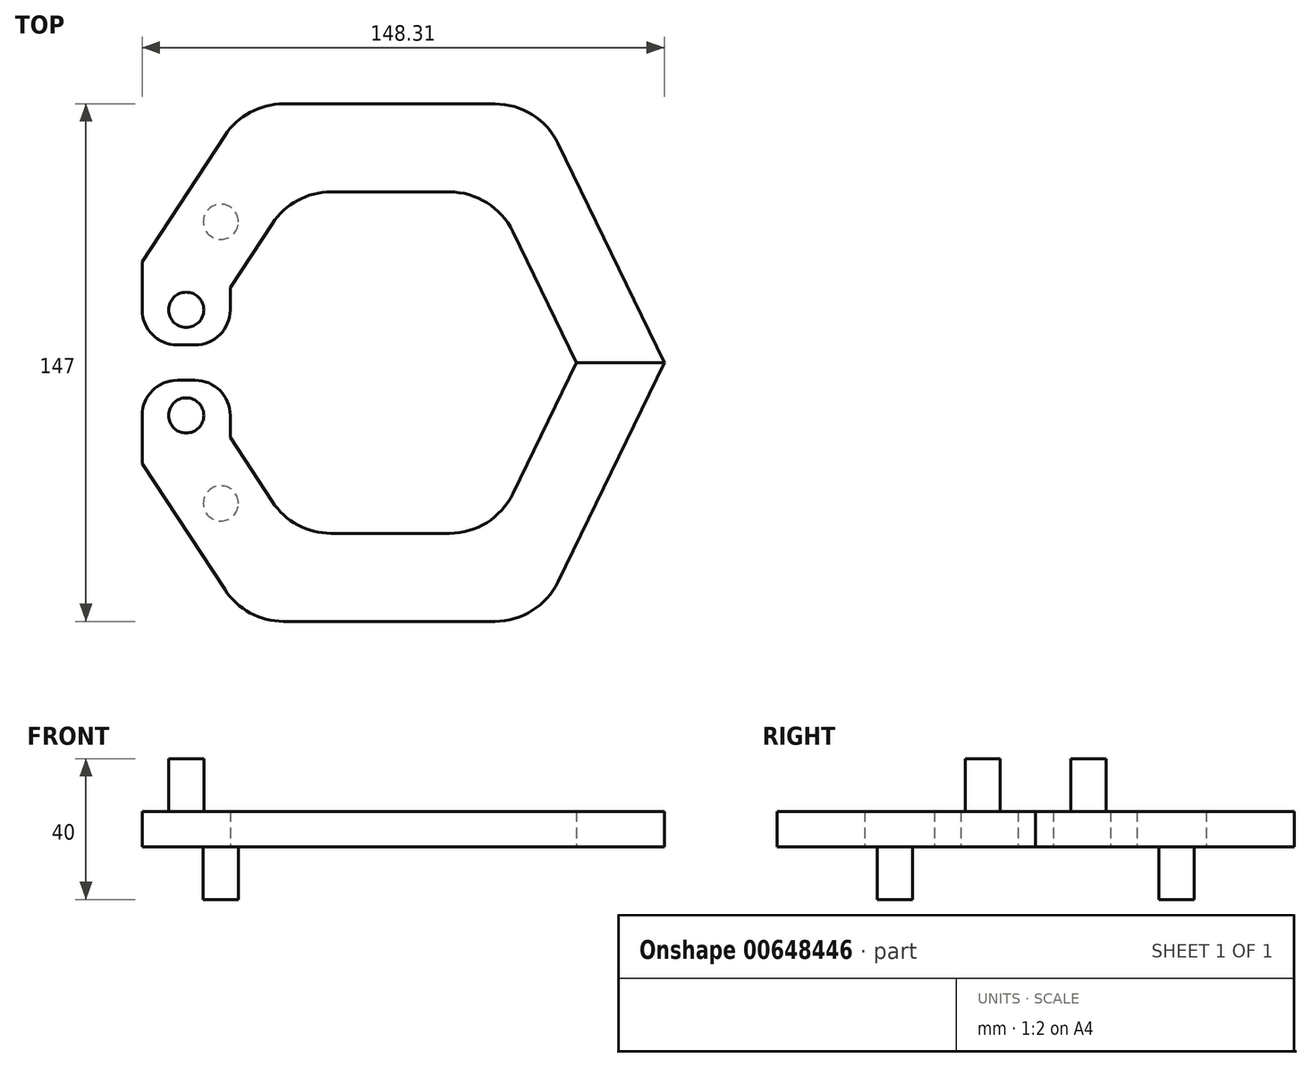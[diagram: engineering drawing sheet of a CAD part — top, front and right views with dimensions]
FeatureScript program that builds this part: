
annotation { "Feature Type Name" : "Feature", "Feature Type Description" : "" }
export const myFeature = defineFeature(function(context is Context, id is Id, definition is map)
    precondition{}
    {
        {
            var Q0;
            Q0=qCreatedBy(makeId("Top.planeOp"),FACE);
            var sketch = newSketch(context, id + "F0", { "sketchPlane" : qUnion([Q0])});
            skLineSegment(sketch, "E0", {"start": v(42.88, -48.5) * mm, "end": v(99.83, -48.5) * mm});
            skLineSegment(sketch, "E1", {"start": v(99.83, -48.5) * mm, "end": v(123.31, 0) * mm});
            skLineSegment(sketch, "E2", {"start": v(123.31, 0) * mm, "end": v(148.31, 0) * mm});
            skLineSegment(sketch, "E3", {"start": v(148.31, 0) * mm, "end": v(112.72, -73.5) * mm});
            skLineSegment(sketch, "E4", {"start": v(112.72, -73.5) * mm, "end": v(29.39, -73.5) * mm});
            skLineSegment(sketch, "E5", {"start": v(29.39, -73.5) * mm, "end": v(0, -28.74) * mm});
            skLineSegment(sketch, "E6", {"start": v(42.88, -48.5) * mm, "end": v(25, -21.26) * mm});
            skLineSegment(sketch, "E7", {"start": v(25, -21.26) * mm, "end": v(25, -5) * mm});
            skLineSegment(sketch, "E8", {"start": v(0, -28.74) * mm, "end": v(0, -5) * mm});
            skLineSegment(sketch, "E9", {"start": v(0, -5) * mm, "end": v(25, -5) * mm});
            skLineSegment(sketch, "E10", {"start": v(12.5, -5) * mm, "end": v(12.5, -25) * mm, "construction": true});
            skLineSegment(sketch, "E11", {"start": v(12.5, -25) * mm, "end": v(36.86, -62.1) * mm, "construction": true});
            skCircle(sketch, "E12", {"center": v(12.5, -15) * mm, "radius": 5 * mm});
            skCircle(sketch, "E13", {"center": v(22.35, -40) * mm, "radius": 5 * mm});
            skSolve(sketch);
        }
        {
            var Q0;
            Q0=makeQuery(id+"F0.imprint","IMPRINT",FACE,{"disambiguationData":[TD([[makeQuery(id+"F0.imprint","IMPRINT",EDGE,{"derivedFrom":sQuery(id+"F0.wireOp",EDGE,"E0")}),-1.0]])]});
            var Q1;
            Q1=makeQuery(id+"F0.imprint","IMPRINT",FACE,{"disambiguationData":[TD([[makeQuery(id+"F0.imprint","IMPRINT",EDGE,{"derivedFrom":sQuery(id+"F0.wireOp",EDGE,"E13")}),1.0]])]});
            var Q2;
            Q2=makeQuery(id+"F0.imprint","IMPRINT",FACE,{"disambiguationData":[TD([[makeQuery(id+"F0.imprint","IMPRINT",EDGE,{"derivedFrom":sQuery(id+"F0.wireOp",EDGE,"E12")}),1.0]])]});
            extrude(context, id + "F1", {"entities" : qUnion([Q0, Q1, Q2]), "depth" : 10 * mm, "offsetDistance" : 25 * mm});
        }
        {
            var Q0;
            Q0=makeQuery(id+"F0.imprint","IMPRINT",FACE,{"disambiguationData":[TD([[makeQuery(id+"F0.imprint","IMPRINT",EDGE,{"derivedFrom":sQuery(id+"F0.wireOp",EDGE,"E13")}),1.0]])]});
            extrude(context, id + "F2", {"entities" : qUnion([Q0]), "operationType" : NewBodyOperationType.ADD, "oppositeDirection" : true, "depth" : 15 * mm, "offsetDistance" : 25 * mm});
        }
        {
            var Q0;
            Q0=makeQuery(id+"F0.imprint","IMPRINT",FACE,{"disambiguationData":[TD([[makeQuery(id+"F0.imprint","IMPRINT",EDGE,{"derivedFrom":sQuery(id+"F0.wireOp",EDGE,"E12")}),1.0]])]});
            extrude(context, id + "F3", {"entities" : qUnion([Q0]), "operationType" : NewBodyOperationType.ADD, "depth" : 25 * mm, "offsetDistance" : 25 * mm});
        }
        {
            var Q0;
            Q0=makeQuery(id+"F1.opExtrude","SWEPT_BODY",BODY,{"disambiguationData":[OSD([sQuery(id+"F0.wireOp",EDGE,"E0"),sQuery(id+"F0.wireOp",EDGE,"E1"),sQuery(id+"F0.wireOp",EDGE,"E2"),sQuery(id+"F0.wireOp",EDGE,"E3"),sQuery(id+"F0.wireOp",EDGE,"E4"),sQuery(id+"F0.wireOp",EDGE,"E5"),sQuery(id+"F0.wireOp",EDGE,"E6"),sQuery(id+"F0.wireOp",EDGE,"E7"),sQuery(id+"F0.wireOp",EDGE,"E8"),sQuery(id+"F0.wireOp",EDGE,"E9")])]});
            transform(context, id + "F4", {"entities" : qUnion([Q0]), "transformType" : TransformType.TRANSLATION_3D, "dx" : 0 * mm, "dy" : 0 * mm, "dz" : 0 * mm, "makeCopy" : true});
        }
        {
            var Q0;
            Q0=makeQuery(id+"F4.opPattern","COPY",BODY,{"derivedFrom":makeQuery(id+"F1.opExtrude","SWEPT_BODY",BODY,{"disambiguationData":[OSD([sQuery(id+"F0.wireOp",EDGE,"E0"),sQuery(id+"F0.wireOp",EDGE,"E1"),sQuery(id+"F0.wireOp",EDGE,"E2"),sQuery(id+"F0.wireOp",EDGE,"E3"),sQuery(id+"F0.wireOp",EDGE,"E4"),sQuery(id+"F0.wireOp",EDGE,"E5"),sQuery(id+"F0.wireOp",EDGE,"E6"),sQuery(id+"F0.wireOp",EDGE,"E7"),sQuery(id+"F0.wireOp",EDGE,"E8"),sQuery(id+"F0.wireOp",EDGE,"E9")])]}),"instanceName":"1"});
            deleteBodies(context, id + "F5", {"entities" : qUnion([Q0])});
        }
        {
            var Q0;
            Q0=makeQuery(id+"F1.opExtrude","SWEPT_BODY",BODY,{"disambiguationData":[OSD([sQuery(id+"F0.wireOp",EDGE,"E0"),sQuery(id+"F0.wireOp",EDGE,"E1"),sQuery(id+"F0.wireOp",EDGE,"E2"),sQuery(id+"F0.wireOp",EDGE,"E3"),sQuery(id+"F0.wireOp",EDGE,"E4"),sQuery(id+"F0.wireOp",EDGE,"E5"),sQuery(id+"F0.wireOp",EDGE,"E6"),sQuery(id+"F0.wireOp",EDGE,"E7"),sQuery(id+"F0.wireOp",EDGE,"E8"),sQuery(id+"F0.wireOp",EDGE,"E9")])]});
            var Q1;
            Q1=qCreatedBy(makeId("Front.planeOp"),FACE);
            mirror(context, id + "F6", {"entities" : qUnion([Q0]), "mirrorPlane" : qUnion([Q1])});
        }
        {
            var Q0;
            Q0=makeQuery(id+"F6.opPattern","COPY",BODY,{"derivedFrom":makeQuery(id+"F1.opExtrude","SWEPT_BODY",BODY,{"disambiguationData":[OSD([sQuery(id+"F0.wireOp",EDGE,"E0"),sQuery(id+"F0.wireOp",EDGE,"E1"),sQuery(id+"F0.wireOp",EDGE,"E2"),sQuery(id+"F0.wireOp",EDGE,"E3"),sQuery(id+"F0.wireOp",EDGE,"E4"),sQuery(id+"F0.wireOp",EDGE,"E5"),sQuery(id+"F0.wireOp",EDGE,"E6"),sQuery(id+"F0.wireOp",EDGE,"E7"),sQuery(id+"F0.wireOp",EDGE,"E8"),sQuery(id+"F0.wireOp",EDGE,"E9")])]}),"instanceName":"1"});
            transform(context, id + "F7", {"entities" : qUnion([Q0]), "transformType" : TransformType.TRANSLATION_3D, "dx" : 0 * mm, "dy" : 0 * mm, "dz" : 0 * mm, "makeCopy" : true});
        }
        {
            var Q0;
            Q0=makeQuery(id+"F7.opPattern","COPY",BODY,{"derivedFrom":makeQuery(id+"F6.opPattern","COPY",BODY,{"derivedFrom":makeQuery(id+"F1.opExtrude","SWEPT_BODY",BODY,{"disambiguationData":[OSD([sQuery(id+"F0.wireOp",EDGE,"E0"),sQuery(id+"F0.wireOp",EDGE,"E1"),sQuery(id+"F0.wireOp",EDGE,"E2"),sQuery(id+"F0.wireOp",EDGE,"E3"),sQuery(id+"F0.wireOp",EDGE,"E4"),sQuery(id+"F0.wireOp",EDGE,"E5"),sQuery(id+"F0.wireOp",EDGE,"E6"),sQuery(id+"F0.wireOp",EDGE,"E7"),sQuery(id+"F0.wireOp",EDGE,"E8"),sQuery(id+"F0.wireOp",EDGE,"E9")])]}),"instanceName":"1"}),"instanceName":"1"});
            deleteBodies(context, id + "F8", {"entities" : qUnion([Q0])});
        }
        {
            var Q0;
            Q0=makeQuery(id+"F6.opPattern","COPY",EDGE,{"derivedFrom":makeQuery(id+"F1.opExtrude","SWEPT_EDGE",EDGE,{"disambiguationData":[OSD([sQuery(id+"F0.wireOp",EDGE,"E8"),sQuery(id+"F0.wireOp",EDGE,"E9")])]}),"instanceName":"1"});
            var Q1;
            Q1=makeQuery(id+"F6.opPattern","COPY",EDGE,{"derivedFrom":makeQuery(id+"F1.opExtrude","SWEPT_EDGE",EDGE,{"disambiguationData":[OSD([sQuery(id+"F0.wireOp",EDGE,"E7"),sQuery(id+"F0.wireOp",EDGE,"E9")])]}),"instanceName":"1"});
            var Q2;
            Q2=makeQuery(id+"F1.opExtrude","SWEPT_EDGE",EDGE,{"disambiguationData":[OSD([sQuery(id+"F0.wireOp",EDGE,"E8"),sQuery(id+"F0.wireOp",EDGE,"E9")])]});
            var Q3;
            Q3=makeQuery(id+"F1.opExtrude","SWEPT_EDGE",EDGE,{"disambiguationData":[OSD([sQuery(id+"F0.wireOp",EDGE,"E7"),sQuery(id+"F0.wireOp",EDGE,"E9")])]});
            fillet(context, id + "F9", {"entities" : qUnion([Q0, Q1, Q2, Q3]), "radius" : 10 * mm, "tangentPropagation" : true, "allowEdgeOverflow" : false});
        }
        {
            var Q0;
            Q0=makeQuery(id+"F6.opPattern","COPY",EDGE,{"derivedFrom":makeQuery(id+"F1.opExtrude","SWEPT_EDGE",EDGE,{"disambiguationData":[OSD([sQuery(id+"F0.wireOp",EDGE,"E0"),sQuery(id+"F0.wireOp",EDGE,"E6")])]}),"instanceName":"1"});
            var Q1;
            Q1=makeQuery(id+"F6.opPattern","COPY",EDGE,{"derivedFrom":makeQuery(id+"F1.opExtrude","SWEPT_EDGE",EDGE,{"disambiguationData":[OSD([sQuery(id+"F0.wireOp",EDGE,"E0"),sQuery(id+"F0.wireOp",EDGE,"E1")])]}),"instanceName":"1"});
            var Q2;
            Q2=makeQuery(id+"F1.opExtrude","SWEPT_EDGE",EDGE,{"disambiguationData":[OSD([sQuery(id+"F0.wireOp",EDGE,"E0"),sQuery(id+"F0.wireOp",EDGE,"E1")])]});
            var Q3;
            Q3=makeQuery(id+"F1.opExtrude","SWEPT_EDGE",EDGE,{"disambiguationData":[OSD([sQuery(id+"F0.wireOp",EDGE,"E0"),sQuery(id+"F0.wireOp",EDGE,"E6")])]});
            var Q4;
            Q4=makeQuery(id+"F6.opPattern","COPY",EDGE,{"derivedFrom":makeQuery(id+"F1.opExtrude","SWEPT_EDGE",EDGE,{"disambiguationData":[OSD([sQuery(id+"F0.wireOp",EDGE,"E4"),sQuery(id+"F0.wireOp",EDGE,"E5")])]}),"instanceName":"1"});
            var Q5;
            Q5=makeQuery(id+"F6.opPattern","COPY",EDGE,{"derivedFrom":makeQuery(id+"F1.opExtrude","SWEPT_EDGE",EDGE,{"disambiguationData":[OSD([sQuery(id+"F0.wireOp",EDGE,"E3"),sQuery(id+"F0.wireOp",EDGE,"E4")])]}),"instanceName":"1"});
            var Q6;
            Q6=makeQuery(id+"F1.opExtrude","SWEPT_EDGE",EDGE,{"disambiguationData":[OSD([sQuery(id+"F0.wireOp",EDGE,"E4"),sQuery(id+"F0.wireOp",EDGE,"E5")])]});
            var Q7;
            Q7=makeQuery(id+"F1.opExtrude","SWEPT_EDGE",EDGE,{"disambiguationData":[OSD([sQuery(id+"F0.wireOp",EDGE,"E3"),sQuery(id+"F0.wireOp",EDGE,"E4")])]});
            fillet(context, id + "F10", {"entities" : qUnion([Q0, Q1, Q2, Q3, Q4, Q5, Q6, Q7]), "radius" : 20 * mm, "tangentPropagation" : true, "allowEdgeOverflow" : false});
        }
    });
